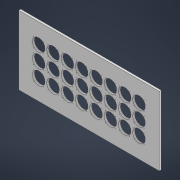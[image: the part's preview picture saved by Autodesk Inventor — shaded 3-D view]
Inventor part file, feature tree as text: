
AUTODESK INVENTOR PART (.ipt)
format: ipt  version: 2021 (Build 250183000, 183)  size: 262,656 bytes
history: native  units: mm
features: sketch x4, hole x3, plane x3, extrude x1, pattern_linear x1
ambient origin geometry x8: Origin, YZ Plane, XZ Plane, XY Plane, X Axis, Y Axis, Z Axis, Center Point
bodies: Solid1 (feature_tree)
feature tree (12):
  extrude  "Extrusion1"  Depth=505.0mm
  hole  "Hole1"  [1 undecoded]
  hole  "Hole2"  [1 undecoded]
  pattern_linear  "Rectangular Pattern1"  Spacing1=369.0mm  [1 undecoded]
  hole  "Hole3"  [1 undecoded]
  plane  "Work Plane1"
  plane  "Work Plane2"
  plane  "Work Plane3"
  sketch  "Sketch1"  dims[d0=1030.0mm d1=505.0mm]
  sketch  "Sketch2"  dims[d2=15.0mm d3=0.0mm d4=147.0mm]
  sketch  "Sketch3"  dims[d5=147.0mm]
  sketch  "Sketch4"  dims[d6=92.0mm d7=6.0mm d8=4.0mm d9=2.0mm d10=90.0deg d11=8.0mm d12=20.594885mm d15=2.8mm d16=6.0mm d17=4.0mm d18=2.0mm d19=90.0deg d20=8.0mm d21=20.594885mm d22=80.0mm d24=105.0mm d25=30.0mm d27=105.0mm d29=3.0mm d30=6.0mm d31=4.0mm d32=2.0mm d33=90.0deg d34=8.0mm d35=20.594885mm d39=369.0mm d40=105.0mm d41=45.0deg d42=40.0mm d44=360.0deg d46=895.0mm d47=-68.0mm]
note: 4 required parameter values undecoded (feature->parameter linkage not recoverable at this tier; creation-order binding heuristic only, values carry confidence <= 0.55)
